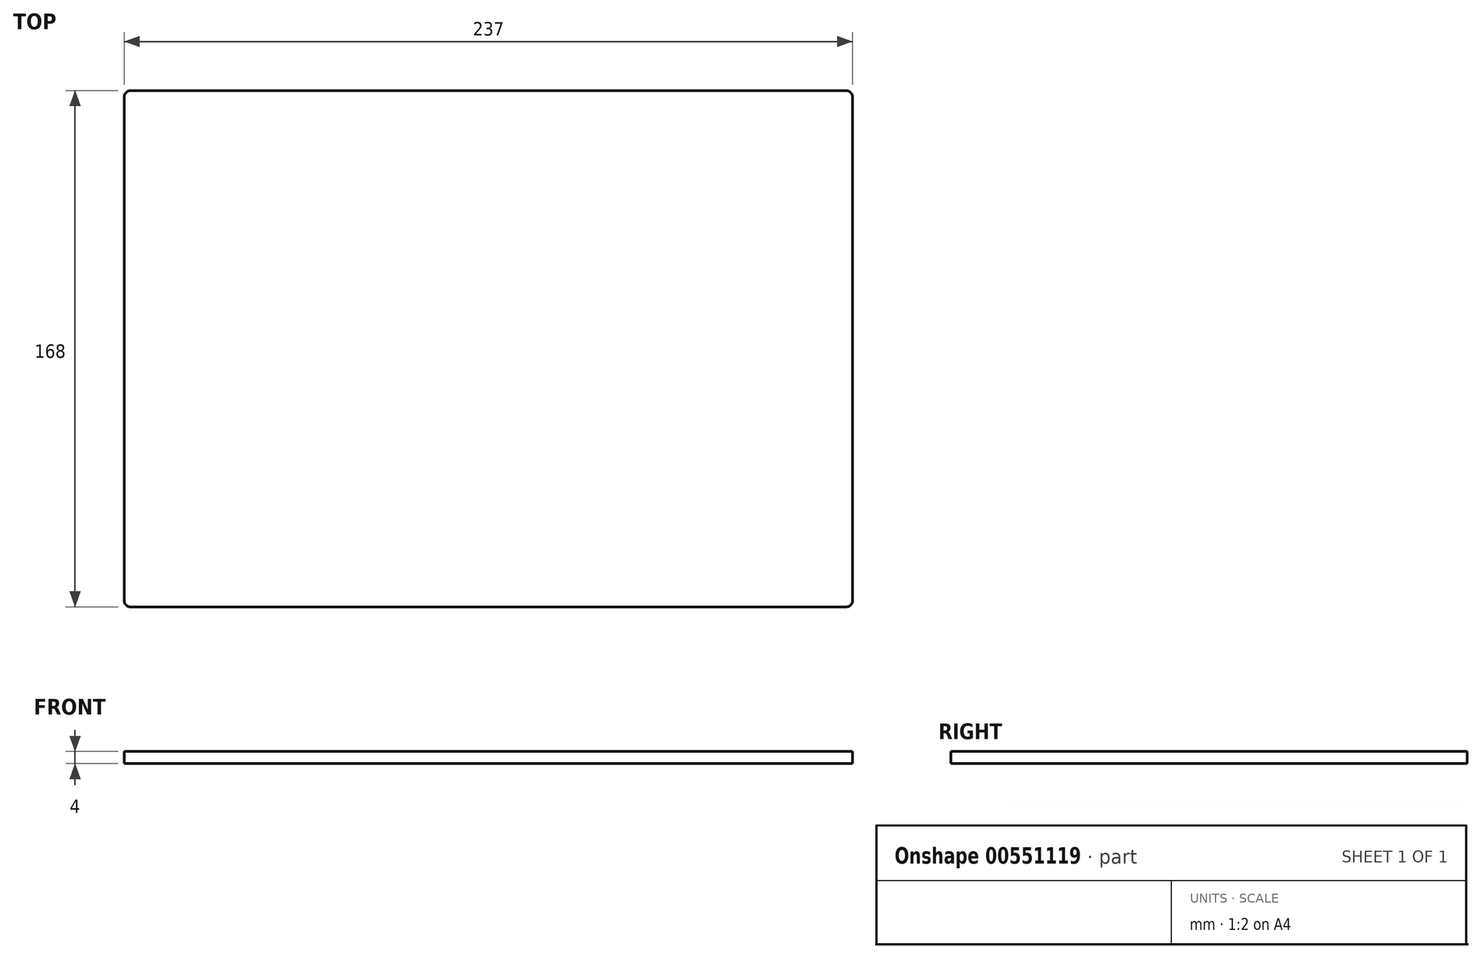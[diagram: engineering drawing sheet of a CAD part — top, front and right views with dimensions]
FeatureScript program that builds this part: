
annotation { "Feature Type Name" : "Feature", "Feature Type Description" : "" }
export const myFeature = defineFeature(function(context is Context, id is Id, definition is map)
    precondition{}
    {
        {
            var Q0;
            Q0=qCreatedBy(makeId("Top.planeOp"),FACE);
            var sketch = newSketch(context, id + "F0", { "sketchPlane" : qUnion([Q0])});
            skLineSegment(sketch, "E0.bottom", {"start": v(-118.5, -84) * mm, "end": v(118.5, -84) * mm});
            skLineSegment(sketch, "E0.top", {"start": v(-118.5, 84) * mm, "end": v(118.5, 84) * mm});
            skLineSegment(sketch, "E0.left", {"start": v(-118.5, -84) * mm, "end": v(-118.5, 84) * mm});
            skLineSegment(sketch, "E0.right", {"start": v(118.5, -84) * mm, "end": v(118.5, 84) * mm});
            skPoint(sketch, "E0.middle", {"position": v(0, 0) * mm});
            skSolve(sketch);
        }
        {
            var Q0;
            Q0 = qSketchRegion(id + "F0", true);
            var Q1;
            Q1=makeQuery(id+"F0.imprint","IMPRINT",FACE,{"disambiguationData":[TD([[makeQuery(id+"F0.imprint","IMPRINT",EDGE,{"derivedFrom":sQuery(id+"F0.wireOp",EDGE,"E0.bottom")}),1.0]])]});
            extrude(context, id + "F1", {"entities" : qUnion([Q0, Q1]), "depth" : 4 * mm, "offsetDistance" : 25 * mm});
        }
        {
            var Q0;
            Q0=makeQuery(id+"F1.opExtrude","SWEPT_EDGE",EDGE,{"disambiguationData":[OSD([sQuery(id+"F0.wireOp",EDGE,"E0.bottom"),sQuery(id+"F0.wireOp",EDGE,"E0.left")])]});
            var Q1;
            Q1=makeQuery(id+"F1.opExtrude","SWEPT_EDGE",EDGE,{"disambiguationData":[OSD([sQuery(id+"F0.wireOp",EDGE,"E0.bottom"),sQuery(id+"F0.wireOp",EDGE,"E0.right")])]});
            var Q2;
            Q2=makeQuery(id+"F1.opExtrude","SWEPT_EDGE",EDGE,{"disambiguationData":[OSD([sQuery(id+"F0.wireOp",EDGE,"E0.top"),sQuery(id+"F0.wireOp",EDGE,"E0.right")])]});
            var Q3;
            Q3=makeQuery(id+"F1.opExtrude","SWEPT_EDGE",EDGE,{"disambiguationData":[OSD([sQuery(id+"F0.wireOp",EDGE,"E0.top"),sQuery(id+"F0.wireOp",EDGE,"E0.left")])]});
            fillet(context, id + "F2", {"entities" : qUnion([Q0, Q1, Q2, Q3]), "radius" : 2 * mm, "tangentPropagation" : true, "allowEdgeOverflow" : false});
        }
    });
